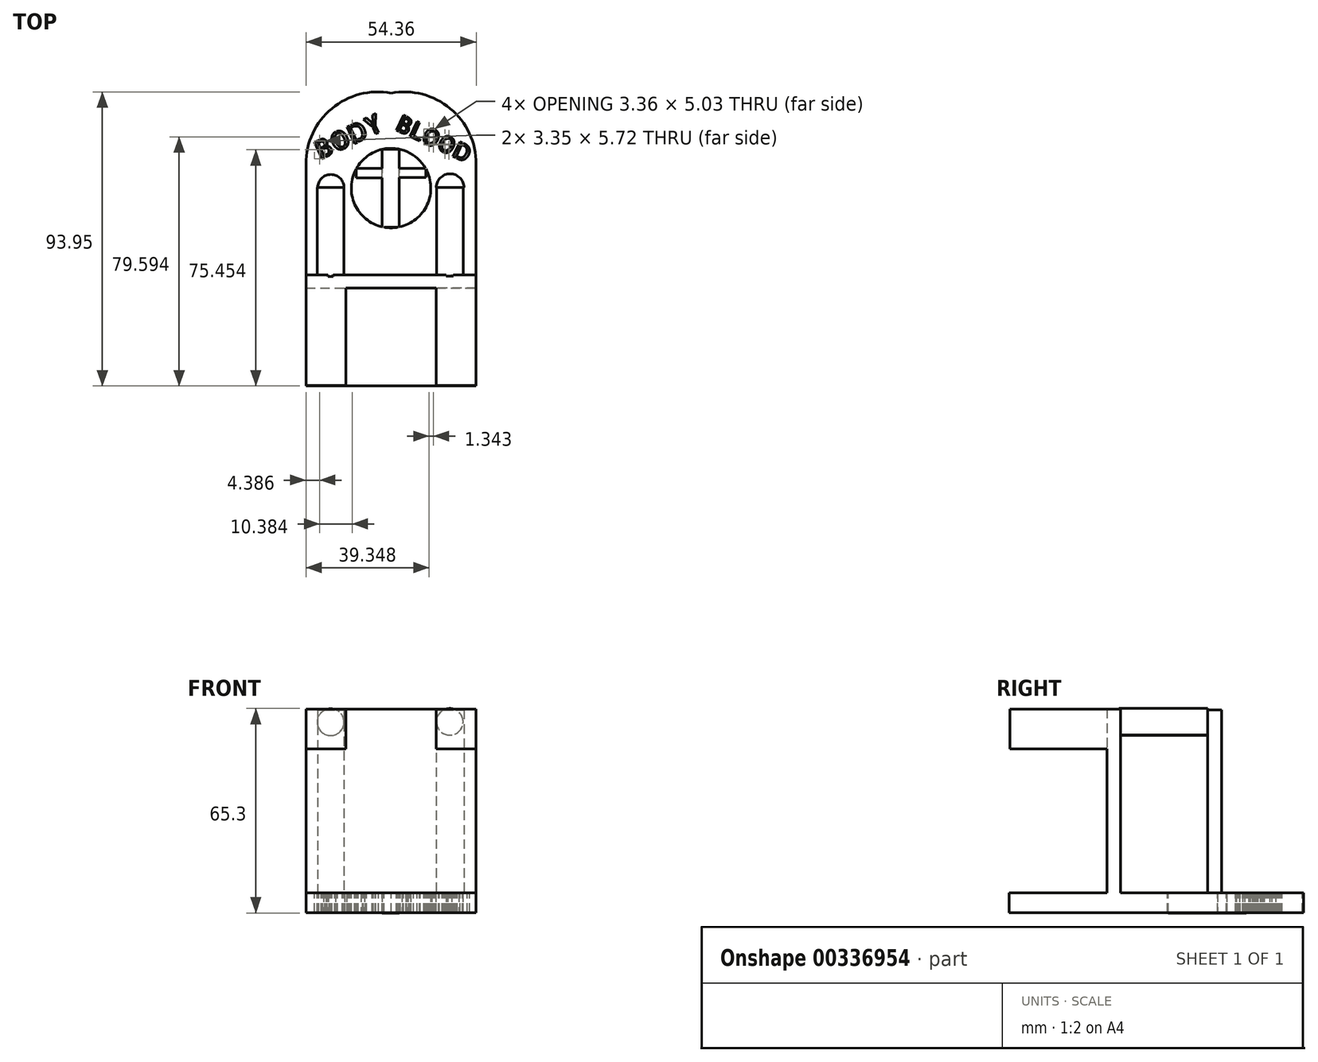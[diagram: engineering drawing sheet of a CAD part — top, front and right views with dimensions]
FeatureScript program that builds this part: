
annotation { "Feature Type Name" : "Feature", "Feature Type Description" : "" }
export const myFeature = defineFeature(function(context is Context, id is Id, definition is map)
    precondition{}
    {
        {
            var Q0;
            Q0=qCreatedBy(makeId("Top.planeOp"),FACE);
            var sketch = newSketch(context, id + "F0", { "sketchPlane" : qUnion([Q0])});
            skLineSegment(sketch, "E0.bottom", {"start": v(27.18, 35.48) * mm, "end": v(-27.18, 35.48) * mm});
            skLineSegment(sketch, "E0.top", {"start": v(27.18, -35.48) * mm, "end": v(-27.18, -35.48) * mm});
            skLineSegment(sketch, "E0.left", {"start": v(27.18, 35.48) * mm, "end": v(27.18, -35.48) * mm});
            skLineSegment(sketch, "E0.right", {"start": v(-27.18, 35.48) * mm, "end": v(-27.18, -35.48) * mm});
            skPoint(sketch, "E0.middle", {"position": v(0, 0) * mm});
            skArc(sketch, "E1", {"start": v(27.18, 35.48) * mm, "mid": v(18.89, 53.15) * mm, "end": v(0, 58.09) * mm});
            skArc(sketch, "E2", {"start": v(-27.18, 35.48) * mm, "mid": v(-18.89, 53.15) * mm, "end": v(0, 58.09) * mm});
            skSolve(sketch);
        }
        {
            var Q0;
            Q0 = qSketchRegion(id + "F0", true);
            extrude(context, id + "F1", {"entities" : qUnion([Q0]), "oppositeDirection" : true, "depth" : 6.35 * mm});
        }
        {
            var Q0;
            Q0=qCreatedBy(makeId("Front.planeOp"),FACE);
            var sketch = newSketch(context, id + "F2", { "sketchPlane" : qUnion([Q0])});
            skLineSegment(sketch, "E3.bottom", {"start": v(-27.18, 0) * mm, "end": v(27.18, 0) * mm});
            skLineSegment(sketch, "E3.top", {"start": v(-27.18, 58.7) * mm, "end": v(27.18, 58.7) * mm});
            skLineSegment(sketch, "E3.left", {"start": v(-27.18, 0) * mm, "end": v(-27.18, 58.7) * mm});
            skLineSegment(sketch, "E3.right", {"start": v(27.18, 0) * mm, "end": v(27.18, 58.7) * mm});
            skSolve(sketch);
        }
        {
            var Q0;
            Q0=makeQuery(id+"F2.imprint","IMPRINT",FACE,{"disambiguationData":[TD([[makeQuery(id+"F2.imprint","IMPRINT",EDGE,{"derivedFrom":sQuery(id+"F2.wireOp",EDGE,"E3.bottom")}),1.0]])]});
            extrude(context, id + "F3", {"entities" : qUnion([Q0]), "operationType" : NewBodyOperationType.ADD, "depth" : 4.24 * mm});
        }
        {
            var Q0;
            Q0=makeQuery(id+"F3.opExtrude","CAP_FACE",FACE,{"disambiguationData":[OSD([sQuery(id+"F2.wireOp",EDGE,"E3.bottom"),sQuery(id+"F2.wireOp",EDGE,"E3.top"),sQuery(id+"F2.wireOp",EDGE,"E3.left"),sQuery(id+"F2.wireOp",EDGE,"E3.right")])],"isStart":false});
            var sketch = newSketch(context, id + "F4", { "sketchPlane" : qUnion([Q0])});
            skLineSegment(sketch, "E4.bottom", {"start": v(-27.18, 58.7) * mm, "end": v(-14.48, 58.7) * mm});
            skLineSegment(sketch, "E4.top", {"start": v(-27.18, 46) * mm, "end": v(-14.48, 46) * mm});
            skLineSegment(sketch, "E4.left", {"start": v(-27.18, 58.7) * mm, "end": v(-27.18, 46) * mm});
            skLineSegment(sketch, "E4.right", {"start": v(-14.48, 58.7) * mm, "end": v(-14.48, 46) * mm});
            skSolve(sketch);
        }
        {
            var Q0;
            Q0 = qSketchRegion(id + "F4", true);
            extrude(context, id + "F5", {"entities" : qUnion([Q0]), "operationType" : NewBodyOperationType.ADD, "depth" : 31.06 * mm});
        }
        {
            var Q0;
            Q0=makeQuery(id+"F3.opExtrude","CAP_FACE",FACE,{"disambiguationData":[OSD([sQuery(id+"F2.wireOp",EDGE,"E3.bottom"),sQuery(id+"F2.wireOp",EDGE,"E3.top"),sQuery(id+"F2.wireOp",EDGE,"E3.left"),sQuery(id+"F2.wireOp",EDGE,"E3.right")])],"isStart":false});
            var sketch = newSketch(context, id + "F6", { "sketchPlane" : qUnion([Q0])});
            skLineSegment(sketch, "E5.bottom", {"start": v(27.18, 58.7) * mm, "end": v(14.48, 58.7) * mm});
            skLineSegment(sketch, "E5.top", {"start": v(27.18, 46) * mm, "end": v(14.48, 46) * mm});
            skLineSegment(sketch, "E5.left", {"start": v(27.18, 58.7) * mm, "end": v(27.18, 46) * mm});
            skLineSegment(sketch, "E5.right", {"start": v(14.48, 58.7) * mm, "end": v(14.48, 46) * mm});
            skSolve(sketch);
        }
        {
            var Q0;
            Q0 = qSketchRegion(id + "F6", true);
            extrude(context, id + "F7", {"entities" : qUnion([Q0]), "operationType" : NewBodyOperationType.ADD, "depth" : 31.04 * mm});
        }
        {
            var Q0;
            {var subQ0=sQuery(id+"F0.wireOp",EDGE,"E2");var subQ2=sQuery(id+"F0.wireOp",EDGE,"E1");var subQ4=sQuery(id+"F0.wireOp",EDGE,"E0.right");var subQ5=sQuery(id+"F0.wireOp",EDGE,"E0.left");Q0=makeQuery(id+"F3.boolean.opBoolean","SPLIT",FACE,{"disambiguationData":[TD([makeQuery(id+"F1.opExtrude","SWEPT_FACE",FACE,{"disambiguationData":[OSD([subQ2])]})])],"derivedFrom":makeQuery(id+"F1.opExtrude","CAP_FACE",FACE,{"disambiguationData":[OSD([sQuery(id+"F0.wireOp",EDGE,"E0.top"),subQ5,subQ4,subQ2,subQ0])],"isStart":true})});}
            var sketch = newSketch(context, id + "F8", { "sketchPlane" : qUnion([Q0])});
            skLineSegment(sketch, "E6", {"start": v(-23.42, 27.89) * mm, "end": v(-15.02, 27.89) * mm});
            skArc(sketch, "E7", {"start": v(-23.42, 27.89) * mm, "mid": v(-19.22, 32.1) * mm, "end": v(-15.02, 27.89) * mm});
            skSolve(sketch);
        }
        {
            var Q0;
            Q0 = qSketchRegion(id + "F8", true);
            extrude(context, id + "F9", {"entities" : qUnion([Q0]), "operationType" : NewBodyOperationType.ADD, "depth" : 58.42 * mm});
        }
        {
            var Q0;
            {var subQ0=sQuery(id+"F0.wireOp",EDGE,"E2");var subQ2=sQuery(id+"F0.wireOp",EDGE,"E1");var subQ4=sQuery(id+"F0.wireOp",EDGE,"E0.right");var subQ5=sQuery(id+"F0.wireOp",EDGE,"E0.left");Q0=makeQuery(id+"F3.boolean.opBoolean","SPLIT",FACE,{"disambiguationData":[TD([makeQuery(id+"F1.opExtrude","SWEPT_FACE",FACE,{"disambiguationData":[OSD([subQ2])]})])],"derivedFrom":makeQuery(id+"F1.opExtrude","CAP_FACE",FACE,{"disambiguationData":[OSD([sQuery(id+"F0.wireOp",EDGE,"E0.top"),subQ5,subQ4,subQ2,subQ0])],"isStart":true})});}
            var sketch = newSketch(context, id + "F10", { "sketchPlane" : qUnion([Q0])});
            skLineSegment(sketch, "E8", {"start": v(14.43, 27.89) * mm, "end": v(23.28, 27.89) * mm});
            skArc(sketch, "E9", {"start": v(14.43, 27.89) * mm, "mid": v(18.86, 32.31) * mm, "end": v(23.28, 27.89) * mm});
            skSolve(sketch);
        }
        {
            var Q0;
            Q0=makeQuery(id+"F10.imprint","IMPRINT",FACE,{"disambiguationData":[TD([[makeQuery(id+"F10.imprint","IMPRINT",EDGE,{"derivedFrom":sQuery(id+"F10.wireOp",EDGE,"E8")}),1.0]])]});
            extrude(context, id + "F11", {"entities" : qUnion([Q0]), "operationType" : NewBodyOperationType.ADD, "depth" : 58.42 * mm});
        }
        {
            var Q0;
            Q0=makeQuery(id+"F9.opExtrude","SWEPT_FACE",FACE,{"disambiguationData":[OSD([sQuery(id+"F8.wireOp",EDGE,"E6")])]});
            var sketch = newSketch(context, id + "F12", { "sketchPlane" : qUnion([Q0])});
            skCircle(sketch, "E10", {"center": v(-19.3, 54.5) * mm, "radius": 4.28 * mm});
            skSolve(sketch);
        }
        {
            var Q0;
            Q0 = qSketchRegion(id + "F12", true);
            extrude(context, id + "F13", {"entities" : qUnion([Q0]), "operationType" : NewBodyOperationType.ADD, "depth" : 28.33 * mm});
        }
        {
            var Q0;
            Q0=makeQuery(id+"F11.opExtrude","SWEPT_FACE",FACE,{"disambiguationData":[OSD([sQuery(id+"F10.wireOp",EDGE,"E8")])]});
            var sketch = newSketch(context, id + "F14", { "sketchPlane" : qUnion([Q0])});
            skCircle(sketch, "E11", {"center": v(18.75, 54.6) * mm, "radius": 4.25 * mm});
            skSolve(sketch);
        }
        {
            var Q0;
            Q0 = qSketchRegion(id + "F14", true);
            extrude(context, id + "F15", {"entities" : qUnion([Q0]), "operationType" : NewBodyOperationType.ADD, "depth" : 28.32 * mm});
        }
        {
            var Q0;
            {var subQ0=sQuery(id+"F0.wireOp",EDGE,"E2");var subQ2=sQuery(id+"F0.wireOp",EDGE,"E1");var subQ4=sQuery(id+"F0.wireOp",EDGE,"E0.right");var subQ5=sQuery(id+"F0.wireOp",EDGE,"E0.left");Q0=makeQuery(id+"F3.boolean.opBoolean","SPLIT",FACE,{"disambiguationData":[TD([makeQuery(id+"F1.opExtrude","SWEPT_FACE",FACE,{"disambiguationData":[OSD([subQ2])]})])],"derivedFrom":makeQuery(id+"F1.opExtrude","CAP_FACE",FACE,{"disambiguationData":[OSD([sQuery(id+"F0.wireOp",EDGE,"E0.top"),subQ5,subQ4,subQ2,subQ0])],"isStart":true})});}
            var sketch = newSketch(context, id + "F16", { "sketchPlane" : qUnion([Q0])});
            skSolve(sketch);
        }
        {
            var Q0;
            {var subQ4=sQuery(id+"F0.wireOp",EDGE,"E1");Q0=makeQuery(id+"F16.imprint","IMPRINT",FACE,{"disambiguationData":[TD([[makeQuery(id+"F16.imprint","IMPRINT",EDGE,{"derivedFrom":makeQuery(id+"F1.opExtrude","CAP_EDGE",EDGE,{"disambiguationData":[OSD([subQ4])],"isStart":true})}),1.0]])]});}
            var sketch = newSketch(context, id + "F17", { "sketchPlane" : qUnion([Q0])});
            skLineSegment(sketch, "E12", {"start": v(0, 27.75) * mm, "end": v(0, 16) * mm});
            skLineSegment(sketch, "E13", {"start": v(0, 16) * mm, "end": v(0, 40) * mm});
            skLineSegment(sketch, "E14", {"start": v(0, 40) * mm, "end": v(0, 27.75) * mm});
            skLineSegment(sketch, "E15", {"start": v(7.45, 27.75) * mm, "end": v(-7.92, 27.75) * mm});
            skLineSegment(sketch, "E16", {"start": v(-7.92, 27.75) * mm, "end": v(0, 16) * mm});
            skLineSegment(sketch, "E17", {"start": v(0, 16) * mm, "end": v(7.45, 27.75) * mm});
            skLineSegment(sketch, "E18", {"start": v(7.45, 27.75) * mm, "end": v(0, 40) * mm});
            skLineSegment(sketch, "E19", {"start": v(0, 40) * mm, "end": v(-7.92, 27.75) * mm});
            skSolve(sketch);
        }
        {
            var Q0;
            Q0=sQuery(id+"F17.wireOp",VERTEX,"E14.end");
            var Q1;
            Q1=makeQuery(id+"F1.opExtrude","SWEPT_BODY",BODY,{"disambiguationData":[OSD([sQuery(id+"F0.wireOp",EDGE,"E0.top"),sQuery(id+"F0.wireOp",EDGE,"E0.left"),sQuery(id+"F0.wireOp",EDGE,"E0.right"),sQuery(id+"F0.wireOp",EDGE,"E1"),sQuery(id+"F0.wireOp",EDGE,"E2")])]});
            hole(context, id + "F18", {"style" : HoleStyle.SIMPLE, "endStyle" : HoleEndStyle.THROUGH, "holeDiameter" : 25.4 * mm, "tappedDepth" : 12.7 * mm, "tapClearance" : 3, "locations" : qUnion([Q0]), "scope" : qUnion([Q1])});
        }
        {
            var Q0;
            {var subQ4=sQuery(id+"F0.wireOp",EDGE,"E1");Q0=makeQuery(id+"F16.imprint","IMPRINT",FACE,{"disambiguationData":[TD([[makeQuery(id+"F16.imprint","IMPRINT",EDGE,{"derivedFrom":makeQuery(id+"F1.opExtrude","CAP_EDGE",EDGE,{"disambiguationData":[OSD([subQ4])],"isStart":true})}),1.0]])]});}
            var sketch = newSketch(context, id + "F19", { "sketchPlane" : qUnion([Q0])});
            skLineSegment(sketch, "E20.bottom", {"start": v(-2.81, 40.15) * mm, "end": v(2.64, 40.15) * mm});
            skLineSegment(sketch, "E20.top", {"start": v(-2.81, 15.25) * mm, "end": v(2.64, 15.25) * mm});
            skLineSegment(sketch, "E20.left", {"start": v(-2.81, 40.15) * mm, "end": v(-2.81, 15.25) * mm});
            skLineSegment(sketch, "E20.right", {"start": v(2.64, 40.15) * mm, "end": v(2.64, 15.25) * mm});
            skSolve(sketch);
        }
        {
            var Q0;
            Q0 = qSketchRegion(id + "F19", true);
            extrude(context, id + "F20", {"entities" : qUnion([Q0]), "operationType" : NewBodyOperationType.ADD, "oppositeDirection" : true, "depth" : 6.45 * mm});
        }
        {
            var Q0;
            {var subQ4=sQuery(id+"F0.wireOp",EDGE,"E1");Q0=makeQuery(id+"F16.imprint","IMPRINT",FACE,{"disambiguationData":[TD([[makeQuery(id+"F16.imprint","IMPRINT",EDGE,{"derivedFrom":makeQuery(id+"F1.opExtrude","CAP_EDGE",EDGE,{"disambiguationData":[OSD([subQ4])],"isStart":true})}),1.0]])]});}
            var sketch = newSketch(context, id + "F21", { "sketchPlane" : qUnion([Q0])});
            skLineSegment(sketch, "E21.bottom", {"start": v(-2.79, 33.98) * mm, "end": v(-11.13, 33.98) * mm});
            skLineSegment(sketch, "E21.top", {"start": v(-2.79, 31.03) * mm, "end": v(-11.13, 31.03) * mm});
            skLineSegment(sketch, "E21.left", {"start": v(-2.79, 33.98) * mm, "end": v(-2.79, 31.03) * mm});
            skLineSegment(sketch, "E21.right", {"start": v(-11.13, 33.98) * mm, "end": v(-11.13, 31.03) * mm});
            skSolve(sketch);
        }
        {
            var Q0;
            Q0 = qSketchRegion(id + "F21", true);
            extrude(context, id + "F22", {"entities" : qUnion([Q0]), "operationType" : NewBodyOperationType.ADD, "oppositeDirection" : true, "depth" : 6.4 * mm});
        }
        {
            var Q0;
            {var subQ4=sQuery(id+"F0.wireOp",EDGE,"E1");Q0=makeQuery(id+"F16.imprint","IMPRINT",FACE,{"disambiguationData":[TD([[makeQuery(id+"F16.imprint","IMPRINT",EDGE,{"derivedFrom":makeQuery(id+"F1.opExtrude","CAP_EDGE",EDGE,{"disambiguationData":[OSD([subQ4])],"isStart":true})}),1.0]])]});}
            var sketch = newSketch(context, id + "F23", { "sketchPlane" : qUnion([Q0])});
            skLineSegment(sketch, "E22.bottom", {"start": v(2.6, 34.04) * mm, "end": v(11.16, 34.04) * mm});
            skLineSegment(sketch, "E22.top", {"start": v(2.6, 31.1) * mm, "end": v(11.16, 31.1) * mm});
            skLineSegment(sketch, "E22.left", {"start": v(2.6, 34.04) * mm, "end": v(2.6, 31.1) * mm});
            skLineSegment(sketch, "E22.right", {"start": v(11.16, 34.04) * mm, "end": v(11.16, 31.1) * mm});
            skSolve(sketch);
        }
        {
            var Q0;
            Q0 = qSketchRegion(id + "F23", true);
            extrude(context, id + "F24", {"entities" : qUnion([Q0]), "operationType" : NewBodyOperationType.ADD, "oppositeDirection" : true, "depth" : 6.35 * mm});
        }
        {
            var Q0;
            {var subQ4=sQuery(id+"F0.wireOp",EDGE,"E1");Q0=makeQuery(id+"F16.imprint","IMPRINT",FACE,{"disambiguationData":[TD([[makeQuery(id+"F16.imprint","IMPRINT",EDGE,{"derivedFrom":makeQuery(id+"F1.opExtrude","CAP_EDGE",EDGE,{"disambiguationData":[OSD([subQ4])],"isStart":true})}),1.0]])]});}
            var sketch = newSketch(context, id + "F25", { "sketchPlane" : qUnion([Q0])});
            skText(sketch, "E23", { "text": "BODY", "fontName": "AllertaStencil-Regular.ttf"});
            const initialGuessF25  = {"E23": [-0.02268, 0.03679, 0.9063, 0.42262, 0.00587]};
            skSetInitialGuess(sketch, initialGuessF25);
            skSolve(sketch);
        }
        {
            var Q0;
            Q0 = qSketchRegion(id + "F25", true);
            extrude(context, id + "F26", {"entities" : qUnion([Q0]), "operationType" : NewBodyOperationType.REMOVE, "oppositeDirection" : true, "depth" : 25.4 * mm});
        }
        {
            var Q0;
            {var subQ4=sQuery(id+"F0.wireOp",EDGE,"E1");Q0=makeQuery(id+"F16.imprint","IMPRINT",FACE,{"disambiguationData":[TD([[makeQuery(id+"F16.imprint","IMPRINT",EDGE,{"derivedFrom":makeQuery(id+"F1.opExtrude","CAP_EDGE",EDGE,{"disambiguationData":[OSD([subQ4])],"isStart":true})}),1.0]])]});}
            var sketch = newSketch(context, id + "F27", { "sketchPlane" : qUnion([Q0])});
            skText(sketch, "E24", { "text": "BLOOD", "fontName": "AllertaStencil-Regular.ttf"});
            const initialGuessF27  = {"E24": [0.0011, 0.04652, 0.9063, -0.42262, 0.00527]};
            skSetInitialGuess(sketch, initialGuessF27);
            skSolve(sketch);
        }
        {
            var Q0;
            Q0 = qSketchRegion(id + "F27", true);
            extrude(context, id + "F28", {"entities" : qUnion([Q0]), "operationType" : NewBodyOperationType.REMOVE, "oppositeDirection" : true, "depth" : 25.4 * mm});
        }
    });
